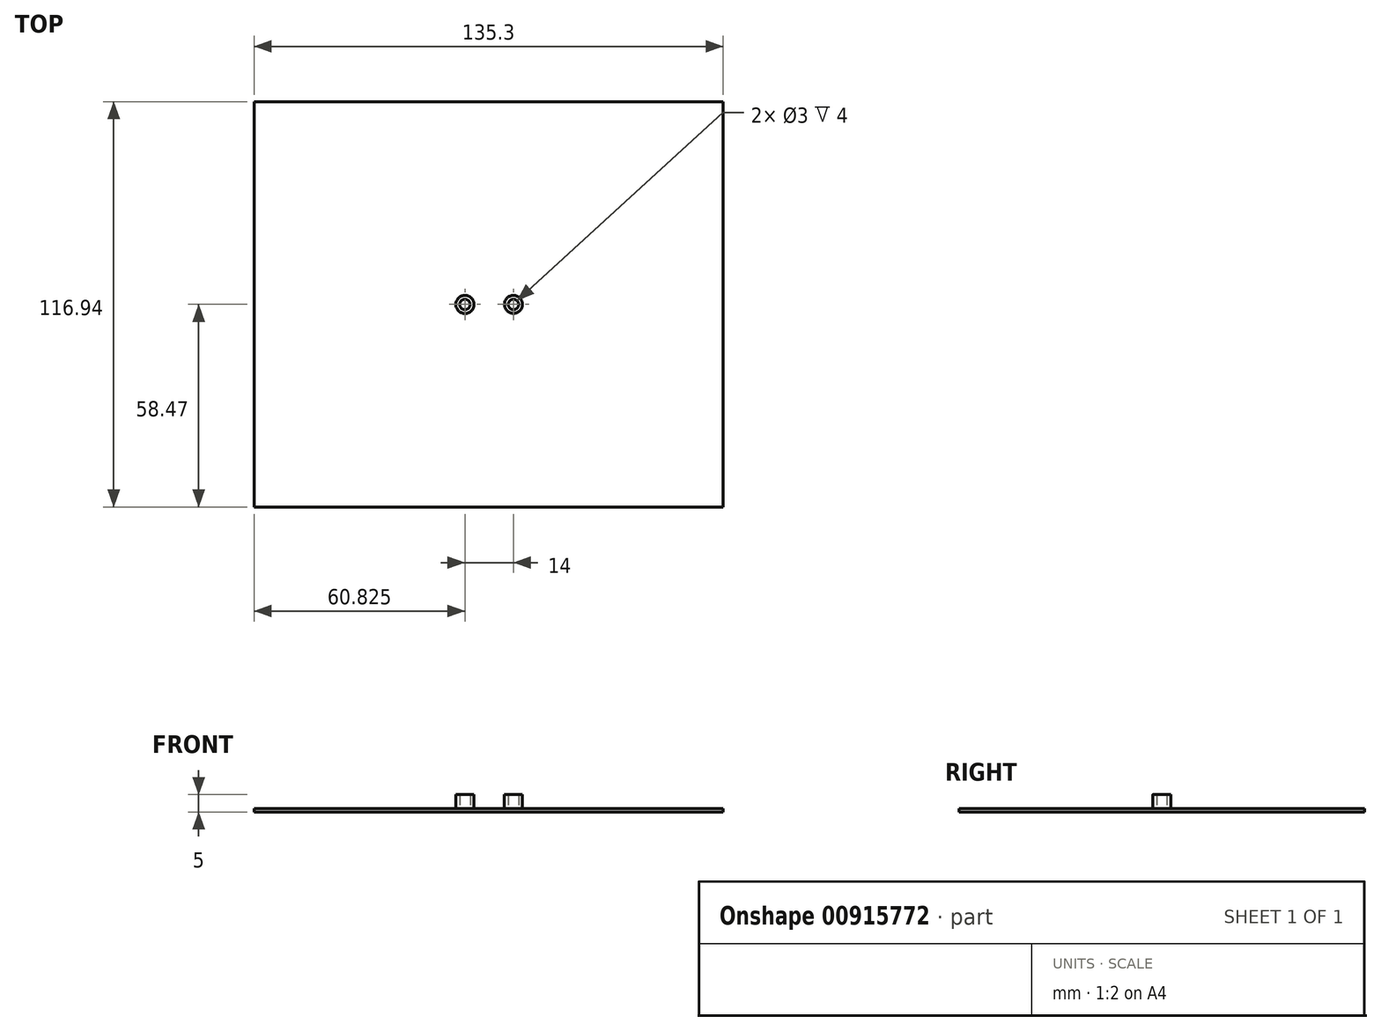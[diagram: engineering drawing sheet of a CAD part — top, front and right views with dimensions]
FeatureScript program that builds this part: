
annotation { "Feature Type Name" : "Feature", "Feature Type Description" : "" }
export const myFeature = defineFeature(function(context is Context, id is Id, definition is map)
    precondition{}
    {
        {
            var Q0;
            Q0=qCreatedBy(makeId("Top.planeOp"),FACE);
            var sketch = newSketch(context, id + "F0", { "sketchPlane" : qUnion([Q0])});
            skLineSegment(sketch, "E0.bottom", {"start": v(67.65, -58.47) * mm, "end": v(-67.65, -58.47) * mm});
            skLineSegment(sketch, "E0.top", {"start": v(67.65, 58.47) * mm, "end": v(-67.65, 58.47) * mm});
            skLineSegment(sketch, "E0.left", {"start": v(67.65, -58.47) * mm, "end": v(67.65, 58.47) * mm});
            skLineSegment(sketch, "E0.right", {"start": v(-67.65, -58.47) * mm, "end": v(-67.65, 58.47) * mm});
            skPoint(sketch, "E0.middle", {"position": v(0, 0) * mm});
            skSolve(sketch);
        }
        {
            var Q0;
            Q0=makeQuery(id+"F0.imprint","IMPRINT",FACE,{"disambiguationData":[TD([[makeQuery(id+"F0.imprint","IMPRINT",EDGE,{"derivedFrom":sQuery(id+"F0.wireOp",EDGE,"E0.bottom")}),-1.0]])]});
            extrude(context, id + "F1", {"entities" : qUnion([Q0]), "depth" : 1 * mm, "offsetDistance" : 25 * mm});
        }
        {
            var Q0;
            Q0=makeQuery(id+"F1.opExtrude","CAP_FACE",FACE,{"disambiguationData":[OSD([sQuery(id+"F0.wireOp",EDGE,"E0.bottom"),sQuery(id+"F0.wireOp",EDGE,"E0.top"),sQuery(id+"F0.wireOp",EDGE,"E0.left"),sQuery(id+"F0.wireOp",EDGE,"E0.right")])],"isStart":false});
            var sketch = newSketch(context, id + "F2", { "sketchPlane" : qUnion([Q0])});
            skCircle(sketch, "E1", {"center": v(-6.83, 0) * mm, "radius": 2.62 * mm});
            skCircle(sketch, "E2", {"center": v(7.17, 0) * mm, "radius": 2.6 * mm});
            skCircle(sketch, "E3", {"center": v(-6.83, 0) * mm, "radius": 1.5 * mm});
            skCircle(sketch, "E4", {"center": v(7.17, 0) * mm, "radius": 1.5 * mm});
            skSolve(sketch);
        }
        {
            var Q0;
            Q0=makeQuery(id+"F2.imprint","IMPRINT",FACE,{"disambiguationData":[TD([[makeQuery(id+"F2.imprint","IMPRINT",EDGE,{"derivedFrom":sQuery(id+"F2.wireOp",EDGE,"E1")}),1.0]])]});
            var Q1;
            Q1=makeQuery(id+"F2.imprint","IMPRINT",FACE,{"disambiguationData":[TD([[makeQuery(id+"F2.imprint","IMPRINT",EDGE,{"derivedFrom":sQuery(id+"F2.wireOp",EDGE,"E2")}),1.0]])]});
            extrude(context, id + "F3", {"entities" : qUnion([Q0, Q1]), "operationType" : NewBodyOperationType.ADD, "depth" : 4 * mm, "offsetDistance" : 25 * mm});
        }
    });
